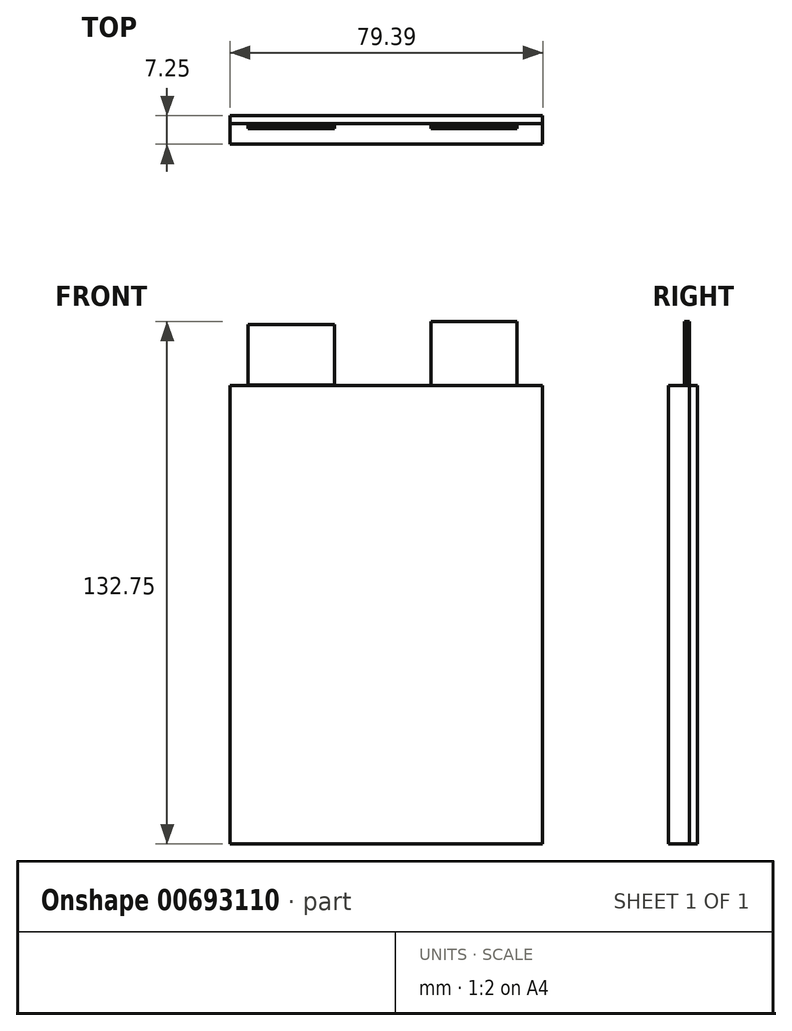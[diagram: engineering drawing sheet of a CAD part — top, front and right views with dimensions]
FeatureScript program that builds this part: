
annotation { "Feature Type Name" : "Feature", "Feature Type Description" : "" }
export const myFeature = defineFeature(function(context is Context, id is Id, definition is map)
    precondition{}
    {
        {
            var Q0;
            Q0=qCreatedBy(makeId("Front.planeOp"),FACE);
            var sketch = newSketch(context, id + "F0", { "sketchPlane" : qUnion([Q0])});
            skLineSegment(sketch, "E0.bottom", {"start": v(28.4, 85.54) * mm, "end": v(-50.98, 85.54) * mm});
            skLineSegment(sketch, "E0.top", {"start": v(28.4, -30.97) * mm, "end": v(-50.98, -30.97) * mm});
            skLineSegment(sketch, "E0.left", {"start": v(28.4, 85.54) * mm, "end": v(28.4, -30.97) * mm});
            skLineSegment(sketch, "E0.right", {"start": v(-50.98, 85.54) * mm, "end": v(-50.98, -30.97) * mm});
            skSolve(sketch);
        }
        {
            var Q0;
            Q0=makeQuery(id+"F0.imprint","IMPRINT",FACE,{"disambiguationData":[TD([[makeQuery(id+"F0.imprint","IMPRINT",EDGE,{"derivedFrom":sQuery(id+"F0.wireOp",EDGE,"E0.bottom")}),1.0]])]});
            var sketch = newSketch(context, id + "F1", { "sketchPlane" : qUnion([Q0])});
            skLineSegment(sketch, "E1.bottom", {"start": v(-45.93, 85.09) * mm, "end": v(-24.48, 85.09) * mm});
            skLineSegment(sketch, "E1.top", {"start": v(-45.93, 101.5) * mm, "end": v(-24.48, 101.5) * mm});
            skLineSegment(sketch, "E1.left", {"start": v(-45.93, 85.09) * mm, "end": v(-45.93, 101.5) * mm});
            skLineSegment(sketch, "E1.right", {"start": v(-24.48, 85.09) * mm, "end": v(-24.48, 101.5) * mm});
            skSolve(sketch);
        }
        {
            var Q0;
            Q0=qCreatedBy(makeId("Front.planeOp"),FACE);
            var sketch = newSketch(context, id + "F2", { "sketchPlane" : qUnion([Q0])});
            skLineSegment(sketch, "E2.bottom", {"start": v(21.89, 85.36) * mm, "end": v(0, 85.36) * mm});
            skLineSegment(sketch, "E2.top", {"start": v(21.89, 101.78) * mm, "end": v(0, 101.78) * mm});
            skLineSegment(sketch, "E2.left", {"start": v(21.89, 85.36) * mm, "end": v(21.89, 101.78) * mm});
            skLineSegment(sketch, "E2.right", {"start": v(0, 85.36) * mm, "end": v(0, 101.78) * mm});
            skSolve(sketch);
        }
        {
            var Q0;
            Q0=makeQuery(id+"F0.imprint","IMPRINT",FACE,{"disambiguationData":[TD([[makeQuery(id+"F0.imprint","IMPRINT",EDGE,{"derivedFrom":sQuery(id+"F0.wireOp",EDGE,"E0.bottom")}),1.0]])]});
            extrude(context, id + "F3", {"entities" : qUnion([Q0]), "depth" : 5.5 * mm, "offsetDistance" : 25 * mm});
        }
        {
            var Q0;
            {var subQ1=sQuery(id+"F1.wireOp",EDGE,"E1.bottom");Q0=makeQuery(id+"F1.imprint","IMPRINT",FACE,{"disambiguationData":[TD([[makeQuery(id+"F1.imprint","IMPRINT",EDGE,{"derivedFrom":subQ1}),-1.0]])]});}
            extrude(context, id + "F4", {"entities" : qUnion([Q0]), "operationType" : NewBodyOperationType.ADD, "depth" : 2.5 * mm, "offsetDistance" : 25 * mm});
        }
        {
            var Q0;
            Q0=makeQuery(id+"F2.imprint","IMPRINT",FACE,{"disambiguationData":[TD([[makeQuery(id+"F2.imprint","IMPRINT",EDGE,{"derivedFrom":sQuery(id+"F2.wireOp",EDGE,"E2.bottom")}),-1.0]])]});
            var sketch = newSketch(context, id + "F5", { "sketchPlane" : qUnion([Q0])});
            skLineSegment(sketch, "E3.bottom", {"start": v(-46.43, 85.55) * mm, "end": v(-24.5, 85.55) * mm});
            skLineSegment(sketch, "E3.top", {"start": v(-46.43, 100.95) * mm, "end": v(-24.5, 100.95) * mm});
            skLineSegment(sketch, "E3.left", {"start": v(-46.43, 85.55) * mm, "end": v(-46.43, 100.95) * mm});
            skLineSegment(sketch, "E3.right", {"start": v(-24.5, 85.55) * mm, "end": v(-24.5, 100.95) * mm});
            skSolve(sketch);
        }
        {
            var Q0;
            Q0=makeQuery(id+"F3.opExtrude","CAP_FACE",FACE,{"disambiguationData":[OSD([sQuery(id+"F0.wireOp",EDGE,"E0.bottom"),sQuery(id+"F0.wireOp",EDGE,"E0.top"),sQuery(id+"F0.wireOp",EDGE,"E0.left"),sQuery(id+"F0.wireOp",EDGE,"E0.right")])],"isStart":true});
            extrude(context, id + "F6", {"entities" : qUnion([Q0]), "depth" : 2 * mm, "offsetDistance" : 25 * mm});
        }
        {
            var Q0;
            Q0=makeQuery(id+"F5.imprint","IMPRINT",FACE,{"disambiguationData":[TD([[makeQuery(id+"F5.imprint","IMPRINT",EDGE,{"derivedFrom":sQuery(id+"F5.wireOp",EDGE,"E3.bottom")}),1.0]])]});
            var Q1;
            Q1=makeQuery(id+"F2.imprint","IMPRINT",FACE,{"disambiguationData":[TD([[makeQuery(id+"F2.imprint","IMPRINT",EDGE,{"derivedFrom":sQuery(id+"F2.wireOp",EDGE,"E2.bottom")}),-1.0]])]});
            extrude(context, id + "F7", {"entities" : qUnion([Q0, Q1]), "depth" : 0.8 * mm, "offsetDistance" : 25 * mm});
        }
        {
            var Q0;
            Q0=makeQuery(id+"F7.opExtrude","CAP_FACE",FACE,{"disambiguationData":[OSD([sQuery(id+"F2.wireOp",EDGE,"E2.bottom"),sQuery(id+"F2.wireOp",EDGE,"E2.top"),sQuery(id+"F2.wireOp",EDGE,"E2.left"),sQuery(id+"F2.wireOp",EDGE,"E2.right")])],"isStart":false});
            var Q1;
            Q1=makeQuery(id+"F7.opExtrude","CAP_FACE",FACE,{"disambiguationData":[OSD([sQuery(id+"F5.wireOp",EDGE,"E3.bottom"),sQuery(id+"F5.wireOp",EDGE,"E3.top"),sQuery(id+"F5.wireOp",EDGE,"E3.left"),sQuery(id+"F5.wireOp",EDGE,"E3.right")])],"isStart":false});
            extrude(context, id + "F8", {"entities" : qUnion([Q0, Q1]), "depth" : 0.5 * mm, "offsetDistance" : 25 * mm});
        }
        {
            var Q0;
            Q0=makeQuery(id+"F3.opExtrude","CAP_FACE",FACE,{"disambiguationData":[OSD([sQuery(id+"F0.wireOp",EDGE,"E0.bottom"),sQuery(id+"F0.wireOp",EDGE,"E0.top"),sQuery(id+"F0.wireOp",EDGE,"E0.left"),sQuery(id+"F0.wireOp",EDGE,"E0.right")])],"isStart":false});
            extrude(context, id + "F9", {"entities" : qUnion([Q0]), "operationType" : NewBodyOperationType.REMOVE, "oppositeDirection" : true, "depth" : .25 * mm, "offsetDistance" : 25 * mm});
        }
    });
